# Revit family: Faucet-Wall_Mounted-American_Standard-Yoke-8344.212
name_source: partatom
category: Plumbing Fixtures
units: mm (PartAtom-declared; Revit-internal decimal feet)

## family parameters
Cut with Voids When Loaded = No
Host = Face
OmniClass Number = 23.45.55.17
OmniClass Title = Mixing Faucets
Part Type = Normal
Room Calculation Point = No
Round Connector Dimension = Use Diameter
Shared = Yes

## types (1)
- 8344.212
    ATS URL = http://www.atsspec.com
    Assembly Code = D2020
    CW Connection = Yes
    CWFU = 1.5
    Cold Water Connection Diameter = 1/2"
    Default Elevation = 0"
    Description = Exposed Yoke Wall-Mount Utility Faucet With Top brace.
    Finish = Brass-American Standard-002-Polished Chrome
    HW Connection = Yes
    HWFU = 1.5
    Height = 2 1/2"
    Hot Water Connection Diameter = 1/2"
    Installation Type = Wall Mounted
    Length = 12 1/2"
    Manufacturer = American Standard
    Material = Brass-American Standard-002-Polished Chrome
    Model = 8344.212
    Omniclass Table 23 Code = 23.45.55.17
    Omniclass Table 23 Title = Mixing Faucets
    Price = Prices may vary. Please consult Manufacturer Representative for most up-to-date price list.
    Product Documentation Link = https://www.americanstandard-us.com
    Product Page URL = http://www.americanstandard-us.com
    Revised Date = 03/01/2021
    Specification = Exposed Yoke Wall-Mount Utility Faucet Top brace. 6" cast brass spout with vacuum breaker. Ceramic disc valves. Integral supply stops. Metal lever handles. Bucket hook. 3/4" threaded hose end. 1/2" NPT female inlets. Rough Chrome (004) finish.
    URL = http://www.americanstandard-us.com
    WFU = 0
    Width = 7 1/4"

## geometry (parser evidence)
native form markers: Sweep x2
no freeform markers — native parametric forms only
